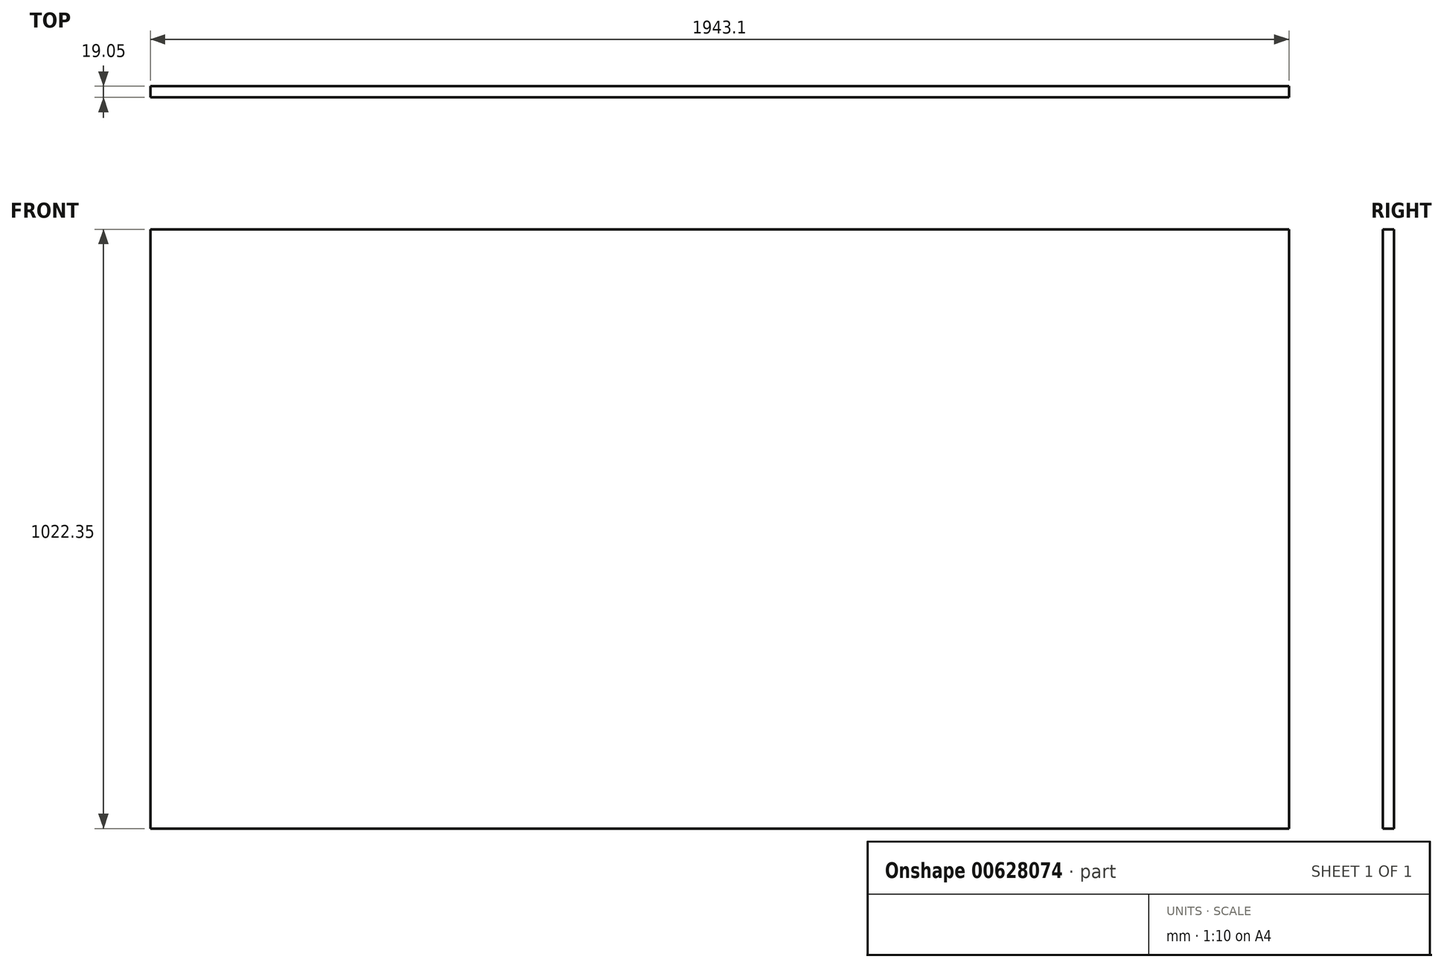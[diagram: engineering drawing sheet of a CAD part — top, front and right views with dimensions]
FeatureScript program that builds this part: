
annotation { "Feature Type Name" : "Feature", "Feature Type Description" : "" }
export const myFeature = defineFeature(function(context is Context, id is Id, definition is map)
    precondition{}
    {
        {
            var Q0;
            Q0=qCreatedBy(makeId("Front.planeOp"),FACE);
            var sketch = newSketch(context, id + "F0", { "sketchPlane" : qUnion([Q0])});
            skLineSegment(sketch, "E0.bottom", {"start": v(-990.36, 655.88) * mm, "end": v(952.74, 655.88) * mm});
            skLineSegment(sketch, "E0.top", {"start": v(-990.36, -366.47) * mm, "end": v(952.74, -366.47) * mm});
            skLineSegment(sketch, "E0.left", {"start": v(-990.36, 655.88) * mm, "end": v(-990.36, -366.47) * mm});
            skLineSegment(sketch, "E0.right", {"start": v(952.74, 655.88) * mm, "end": v(952.74, -366.47) * mm});
            skSolve(sketch);
        }
        {
            var Q0;
            Q0 = qSketchRegion(id + "F0", true);
            extrude(context, id + "F1", {"entities" : qUnion([Q0]), "depth" : 19.05 * mm, "offsetDistance" : 25.4 * mm});
        }
    });
